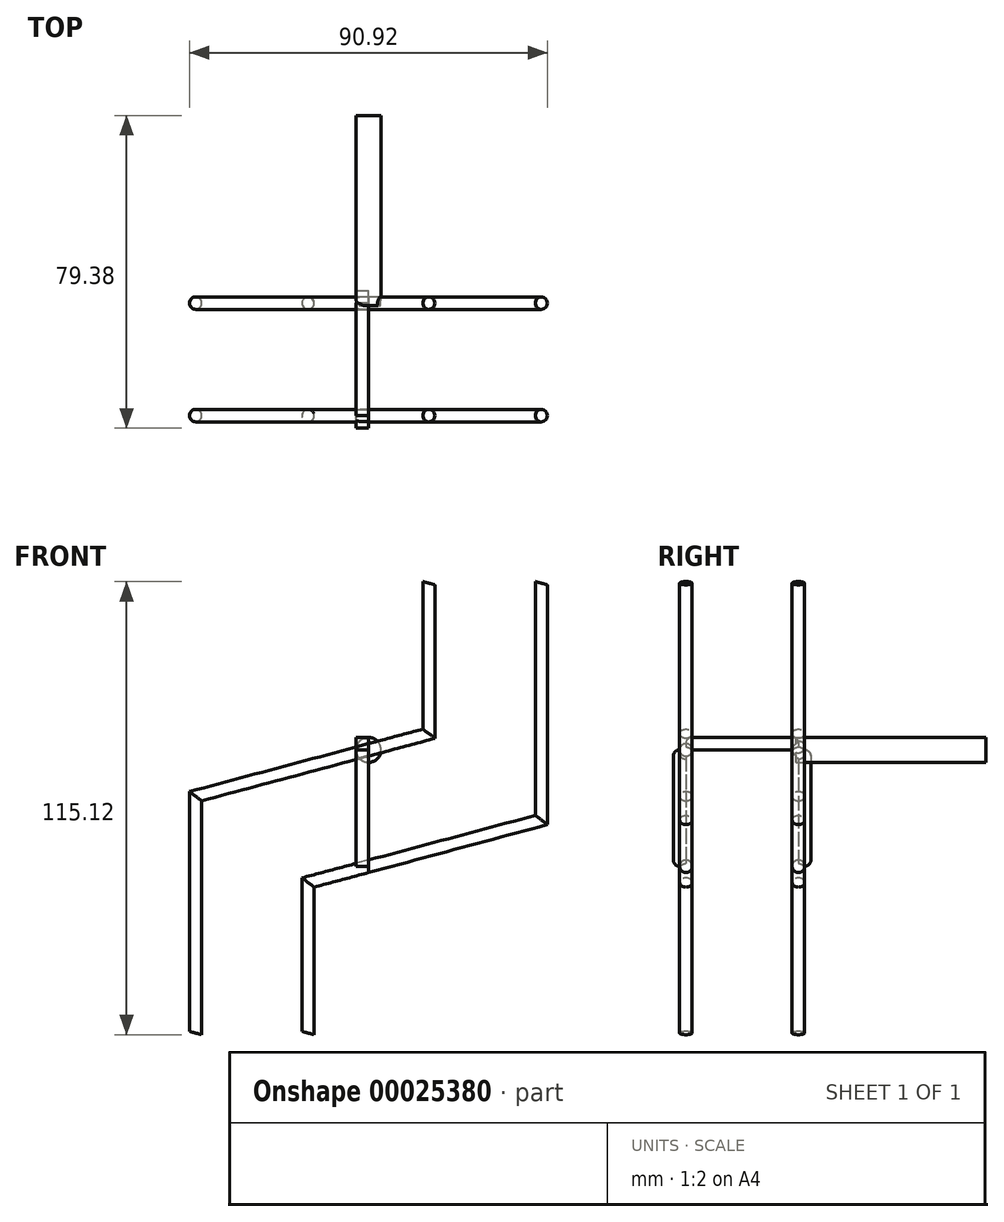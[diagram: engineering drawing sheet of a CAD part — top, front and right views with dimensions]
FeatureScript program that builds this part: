
annotation { "Feature Type Name" : "Feature", "Feature Type Description" : "" }
export const myFeature = defineFeature(function(context is Context, id is Id, definition is map)
    precondition{}
    {
        {
            var Q0;
            Q0=qCreatedBy(makeId("Front.planeOp"),FACE);
            cPlane(context, id + "F0", {"entities" : qUnion([Q0]), "cplaneType" : CPlaneType.OFFSET, "offset" : 76.2 * mm, "width" : 152.4 * mm, "height" : 152.4 * mm});
        }
        {
            var Q0;
            Q0=qCreatedBy(id+"F0.planeOp",FACE);
            var sketch = newSketch(context, id + "F1", { "sketchPlane" : qUnion([Q0])});
            skLineSegment(sketch, "E0", {"start": v(0, 0) * mm, "end": v(-43.92, -11.77) * mm});
            skLineSegment(sketch, "E1", {"start": v(0, 0) * mm, "end": v(15.35, 4.11) * mm});
            skLineSegment(sketch, "E2", {"start": v(-43.92, -11.77) * mm, "end": v(-43.92, -71.94) * mm});
            skLineSegment(sketch, "E3", {"start": v(15.35, 4.11) * mm, "end": v(15.35, 42.36) * mm});
            skLineSegment(sketch, "E4", {"start": v(0, 0) * mm, "end": v(0, 57.51) * mm, "construction": true});
            skLineSegment(sketch, "E5", {"start": v(0, -29.58) * mm, "end": v(-15.35, -33.7) * mm});
            skLineSegment(sketch, "E6", {"start": v(0, -29.58) * mm, "end": v(43.92, -17.81) * mm});
            skLineSegment(sketch, "E7", {"start": v(43.92, -17.81) * mm, "end": v(43.92, 42.36) * mm});
            skLineSegment(sketch, "E8", {"start": v(-15.35, -33.7) * mm, "end": v(-15.35, -71.94) * mm});
            skSolve(sketch);
        }
        {
            var Q0;
            Q0=qCreatedBy(makeId("Right.planeOp"),FACE);
            var sketch = newSketch(context, id + "F2", { "sketchPlane" : qUnion([Q0])});
            skCircle(sketch, "E9", {"center": v(-76.2, 0) * mm, "radius": 1.59 * mm});
            skCircle(sketch, "E10", {"center": v(-76.2, -29.58) * mm, "radius": 1.59 * mm});
            skCircle(sketch, "E11", {"center": v(-47.62, 0) * mm, "radius": 1.59 * mm});
            skCircle(sketch, "E12", {"center": v(-47.62, -29.58) * mm, "radius": 1.59 * mm});
            skLineSegment(sketch, "E13.bottom", {"start": v(-77.8, 0) * mm, "end": v(-76.2, 0) * mm});
            skLineSegment(sketch, "E13.top", {"start": v(-77.8, -29.58) * mm, "end": v(-76.2, -29.58) * mm});
            skLineSegment(sketch, "E13.left", {"start": v(-79.38, -1.57) * mm, "end": v(-79.38, -28) * mm});
            skLineSegment(sketch, "E13.right", {"start": v(-76.2, 0) * mm, "end": v(-76.2, -29.58) * mm});
            skPoint(sketch, "E14.visualSharp", {"position": v(-79.38, 0) * mm});
            skArc(sketch, "E14.filletArc", {"start": v(-77.8, 0) * mm, "mid": v(-78.91, -0.46) * mm, "end": v(-79.38, -1.57) * mm});
            skPoint(sketch, "E15.visualSharp", {"position": v(-79.38, -29.58) * mm});
            skArc(sketch, "E15.filletArc", {"start": v(-79.38, -28) * mm, "mid": v(-78.91, -29.12) * mm, "end": v(-77.8, -29.58) * mm});
            skLineSegment(sketch, "E16.bottom", {"start": v(-74.63, 3.18) * mm, "end": v(-49.2, 3.18) * mm});
            skLineSegment(sketch, "E16.top", {"start": v(-76.2, 0) * mm, "end": v(-47.62, 0) * mm});
            skLineSegment(sketch, "E16.left", {"start": v(-76.2, 1.6) * mm, "end": v(-76.2, 0) * mm});
            skLineSegment(sketch, "E16.right", {"start": v(-47.62, 1.6) * mm, "end": v(-47.62, 0) * mm});
            skLineSegment(sketch, "E17.bottom", {"start": v(-47.62, 0) * mm, "end": v(-46.02, 0) * mm});
            skLineSegment(sketch, "E17.top", {"start": v(-47.62, -29.58) * mm, "end": v(-46.02, -29.58) * mm});
            skLineSegment(sketch, "E17.left", {"start": v(-47.62, 0) * mm, "end": v(-47.62, -29.58) * mm});
            skLineSegment(sketch, "E17.right", {"start": v(-44.45, -1.57) * mm, "end": v(-44.45, -28) * mm});
            skPoint(sketch, "E18.visualSharp", {"position": v(-44.45, 0) * mm});
            skArc(sketch, "E18.filletArc", {"start": v(-44.45, -1.57) * mm, "mid": v(-44.91, -0.46) * mm, "end": v(-46.02, 0) * mm});
            skPoint(sketch, "E19.visualSharp", {"position": v(-44.45, -29.58) * mm});
            skArc(sketch, "E19.filletArc", {"start": v(-46.02, -29.58) * mm, "mid": v(-44.91, -29.12) * mm, "end": v(-44.45, -28) * mm});
            skPoint(sketch, "E20.visualSharp", {"position": v(-76.2, 3.18) * mm});
            skArc(sketch, "E20.filletArc", {"start": v(-74.63, 3.17) * mm, "mid": v(-75.74, 2.71) * mm, "end": v(-76.2, 1.6) * mm});
            skPoint(sketch, "E21.visualSharp", {"position": v(-47.62, 3.18) * mm});
            skArc(sketch, "E21.filletArc", {"start": v(-47.62, 1.6) * mm, "mid": v(-48.09, 2.71) * mm, "end": v(-49.2, 3.18) * mm});
            skSolve(sketch);
        }
        {
            var Q0;
            Q0=makeQuery(id+"F2.imprint","IMPRINT",FACE,{"disambiguationData":[TD([[makeQuery(id+"F2.imprint","IMPRINT",EDGE,{"derivedFrom":sQuery(id+"F2.wireOp",EDGE,"E9")}),1.0]])]});
            var Q1;
            Q1=makeQuery(id+"F2.imprint","IMPRINT",FACE,{"disambiguationData":[TD([[makeQuery(id+"F2.imprint","IMPRINT",EDGE,{"derivedFrom":sQuery(id+"F2.wireOp",EDGE,"E11")}),1.0]])]});
            var Q2;
            Q2=sQuery(id+"F1.wireOp",EDGE,"E1");
            var Q3;
            Q3=sQuery(id+"F1.wireOp",EDGE,"E3");
            sweep(context, id + "F3", {"profiles" : qUnion([Q0, Q1]), "path" : qUnion([Q2, Q3])});
        }
        {
            var Q0;
            Q0=makeQuery(id+"F2.imprint","IMPRINT",FACE,{"disambiguationData":[TD([[makeQuery(id+"F2.imprint","IMPRINT",EDGE,{"derivedFrom":sQuery(id+"F2.wireOp",EDGE,"E9")}),1.0]])]});
            var Q1;
            Q1=makeQuery(id+"F2.imprint","IMPRINT",FACE,{"disambiguationData":[TD([[makeQuery(id+"F2.imprint","IMPRINT",EDGE,{"derivedFrom":sQuery(id+"F2.wireOp",EDGE,"E11")}),1.0]])]});
            var Q2;
            Q2=sQuery(id+"F1.wireOp",EDGE,"E0");
            var Q3;
            Q3=sQuery(id+"F1.wireOp",EDGE,"E2");
            sweep(context, id + "F4", {"operationType" : NewBodyOperationType.ADD, "profiles" : qUnion([Q0, Q1]), "path" : qUnion([Q2, Q3])});
        }
        {
            var Q0;
            Q0=makeQuery(id+"F2.imprint","IMPRINT",FACE,{"disambiguationData":[TD([[makeQuery(id+"F2.imprint","IMPRINT",EDGE,{"derivedFrom":sQuery(id+"F2.wireOp",EDGE,"E10")}),1.0]])]});
            var Q1;
            Q1=makeQuery(id+"F2.imprint","IMPRINT",FACE,{"disambiguationData":[TD([[makeQuery(id+"F2.imprint","IMPRINT",EDGE,{"derivedFrom":sQuery(id+"F2.wireOp",EDGE,"E12")}),1.0]])]});
            var Q2;
            Q2=sQuery(id+"F1.wireOp",EDGE,"E6");
            var Q3;
            Q3=sQuery(id+"F1.wireOp",EDGE,"E7");
            sweep(context, id + "F5", {"profiles" : qUnion([Q0, Q1]), "path" : qUnion([Q2, Q3])});
        }
        {
            var Q0;
            Q0=makeQuery(id+"F2.imprint","IMPRINT",FACE,{"disambiguationData":[TD([[makeQuery(id+"F2.imprint","IMPRINT",EDGE,{"derivedFrom":sQuery(id+"F2.wireOp",EDGE,"E10")}),1.0]])]});
            var Q1;
            Q1=makeQuery(id+"F2.imprint","IMPRINT",FACE,{"disambiguationData":[TD([[makeQuery(id+"F2.imprint","IMPRINT",EDGE,{"derivedFrom":sQuery(id+"F2.wireOp",EDGE,"E12")}),1.0]])]});
            var Q2;
            Q2=sQuery(id+"F1.wireOp",EDGE,"E5");
            var Q3;
            Q3=sQuery(id+"F1.wireOp",EDGE,"E8");
            sweep(context, id + "F6", {"operationType" : NewBodyOperationType.ADD, "profiles" : qUnion([Q0, Q1]), "path" : qUnion([Q2, Q3])});
        }
        {
            var Q0;
            {var subQ1=sQuery(id+"F2.wireOp",EDGE,"E10");var subQ3=sQuery(id+"F2.wireOp",EDGE,"E13.top");var subQ5=makeQuery(id+"F2.imprint","INTERSECT",VERTEX,{"derivedFrom":[subQ1,subQ3]});Q0=makeQuery(id+"F2.imprint","IMPRINT",FACE,{"disambiguationData":[TD([[makeQuery(id+"F2.imprint","IMPRINT",EDGE,{"disambiguationData":[TD([[subQ5,1.0]])],"derivedFrom":subQ1}),1.0]])]});}
            var Q1;
            Q1=makeQuery(id+"F2.imprint","IMPRINT",FACE,{"disambiguationData":[TD([[makeQuery(id+"F2.imprint","IMPRINT",EDGE,{"derivedFrom":sQuery(id+"F2.wireOp",EDGE,"E13.left")}),1.0]])]});
            var Q2;
            {var subQ0=sQuery(id+"F2.wireOp",EDGE,"E13.bottom");var subQ1=sQuery(id+"F2.wireOp",EDGE,"E9");var subQ2=makeQuery(id+"F2.imprint","INTERSECT",VERTEX,{"derivedFrom":[subQ1,subQ0]});Q2=makeQuery(id+"F2.imprint","IMPRINT",FACE,{"disambiguationData":[TD([[makeQuery(id+"F2.imprint","IMPRINT",EDGE,{"disambiguationData":[TD([[subQ2,-1.0]])],"derivedFrom":subQ1}),1.0]])]});}
            var Q3;
            {var subQ0=sQuery(id+"F2.wireOp",EDGE,"E16.left");var subQ1=sQuery(id+"F2.wireOp",EDGE,"E9");var subQ2=makeQuery(id+"F2.imprint","INTERSECT",VERTEX,{"derivedFrom":[subQ1,subQ0]});Q3=makeQuery(id+"F2.imprint","IMPRINT",FACE,{"disambiguationData":[TD([[makeQuery(id+"F2.imprint","IMPRINT",EDGE,{"disambiguationData":[TD([[subQ2,1.0]])],"derivedFrom":subQ1}),1.0]])]});}
            var Q4;
            Q4=makeQuery(id+"F2.imprint","IMPRINT",FACE,{"disambiguationData":[TD([[makeQuery(id+"F2.imprint","IMPRINT",EDGE,{"derivedFrom":sQuery(id+"F2.wireOp",EDGE,"E16.bottom")}),-1.0]])]});
            var Q5;
            {var subQ0=sQuery(id+"F2.wireOp",EDGE,"E16.right");var subQ1=sQuery(id+"F2.wireOp",EDGE,"E11");var subQ2=makeQuery(id+"F2.imprint","INTERSECT",VERTEX,{"derivedFrom":[subQ1,subQ0]});Q5=makeQuery(id+"F2.imprint","IMPRINT",FACE,{"disambiguationData":[TD([[makeQuery(id+"F2.imprint","IMPRINT",EDGE,{"disambiguationData":[TD([[subQ2,-1.0]])],"derivedFrom":subQ1}),1.0]])]});}
            var Q6;
            {var subQ1=sQuery(id+"F2.wireOp",EDGE,"E11");var subQ3=sQuery(id+"F2.wireOp",EDGE,"E17.bottom");var subQ5=makeQuery(id+"F2.imprint","INTERSECT",VERTEX,{"derivedFrom":[subQ1,subQ3]});Q6=makeQuery(id+"F2.imprint","IMPRINT",FACE,{"disambiguationData":[TD([[makeQuery(id+"F2.imprint","IMPRINT",EDGE,{"disambiguationData":[TD([[subQ5,1.0]])],"derivedFrom":subQ1}),1.0]])]});}
            var Q7;
            Q7=makeQuery(id+"F2.imprint","IMPRINT",FACE,{"disambiguationData":[TD([[makeQuery(id+"F2.imprint","IMPRINT",EDGE,{"derivedFrom":sQuery(id+"F2.wireOp",EDGE,"E17.right")}),-1.0]])]});
            var Q8;
            {var subQ1=sQuery(id+"F2.wireOp",EDGE,"E12");var subQ3=sQuery(id+"F2.wireOp",EDGE,"E17.top");var subQ5=makeQuery(id+"F2.imprint","INTERSECT",VERTEX,{"derivedFrom":[subQ1,subQ3]});Q8=makeQuery(id+"F2.imprint","IMPRINT",FACE,{"disambiguationData":[TD([[makeQuery(id+"F2.imprint","IMPRINT",EDGE,{"disambiguationData":[TD([[subQ5,-1.0]])],"derivedFrom":subQ1}),1.0]])]});}
            extrude(context, id + "F7", {"entities" : qUnion([Q0, Q1, Q2, Q3, Q4, Q5, Q6, Q7, Q8]), "operationType" : NewBodyOperationType.ADD, "oppositeDirection" : true, "depth" : 3.17 * mm});
        }
        {
            var Q0;
            Q0=qCreatedBy(makeId("Front.planeOp"),FACE);
            var sketch = newSketch(context, id + "F8", { "sketchPlane" : qUnion([Q0])});
            skCircle(sketch, "E22", {"center": v(0, 0) * mm, "radius": 3.18 * mm});
            skSolve(sketch);
        }
        {
            var Q0;
            Q0=makeQuery(id+"F8.imprint","IMPRINT",FACE,{"disambiguationData":[TD([[makeQuery(id+"F8.imprint","IMPRINT",EDGE,{"derivedFrom":sQuery(id+"F8.wireOp",EDGE,"E22")}),1.0]])]});
            extrude(context, id + "F9", {"entities" : qUnion([Q0]), "operationType" : NewBodyOperationType.ADD, "depth" : 48.26 * mm});
        }
    });
